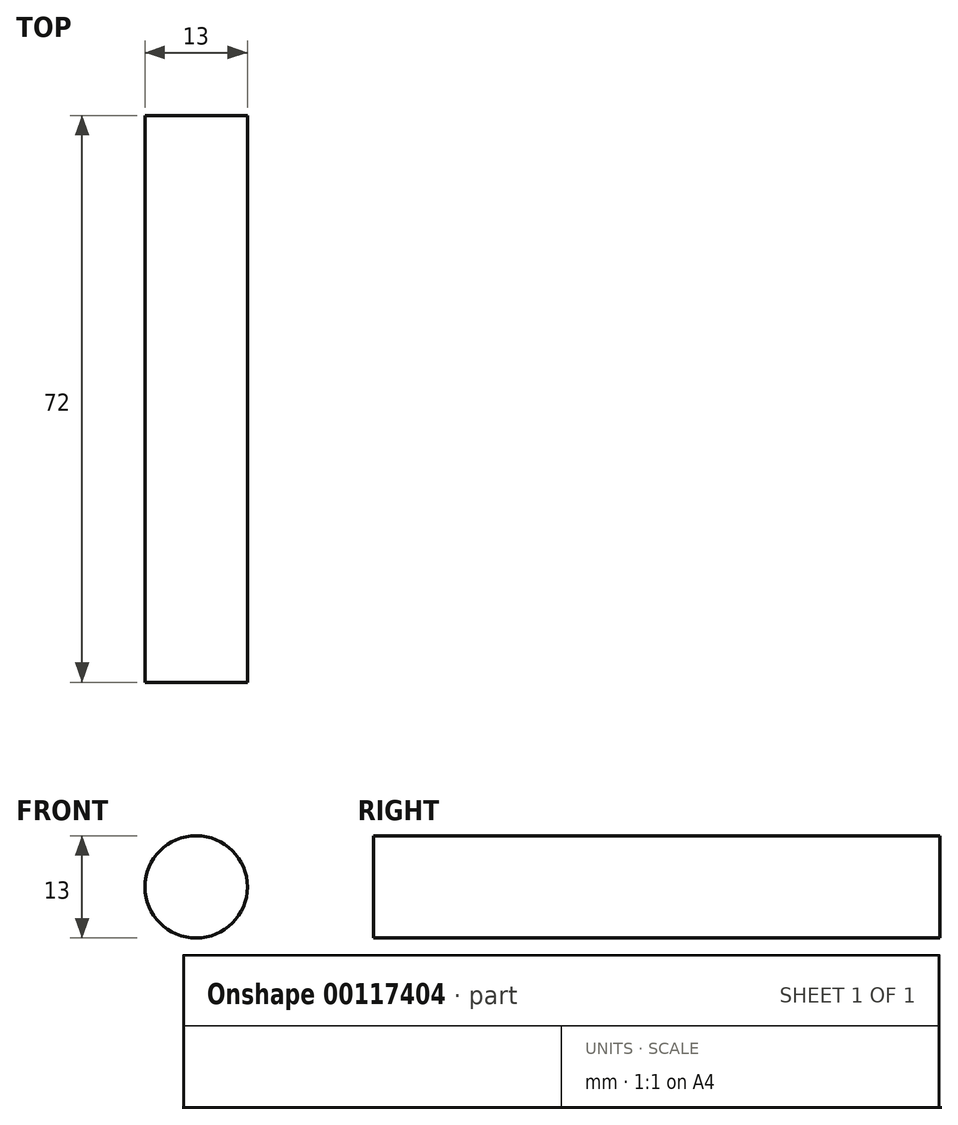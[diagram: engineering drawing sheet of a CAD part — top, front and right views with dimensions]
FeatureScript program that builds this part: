
annotation { "Feature Type Name" : "Feature", "Feature Type Description" : "" }
export const myFeature = defineFeature(function(context is Context, id is Id, definition is map)
    precondition{}
    {
        {
            var Q0;
            Q0=qCreatedBy(makeId("Front.planeOp"),FACE);
            var sketch = newSketch(context, id + "F0", { "sketchPlane" : qUnion([Q0])});
            skCircle(sketch, "E0", {"center": v(-36.41, 27.37) * mm, "radius": 6.5 * mm});
            skSolve(sketch);
        }
        {
            var Q0;
            Q0=makeQuery(id+"F0.imprint","IMPRINT",FACE,{"disambiguationData":[TD([[makeQuery(id+"F0.imprint","IMPRINT",EDGE,{"derivedFrom":sQuery(id+"F0.wireOp",EDGE,"E0")}),1.0]])]});
            extrude(context, id + "F1", {"entities" : qUnion([Q0]), "depth" : 72 * mm});
        }
    });
